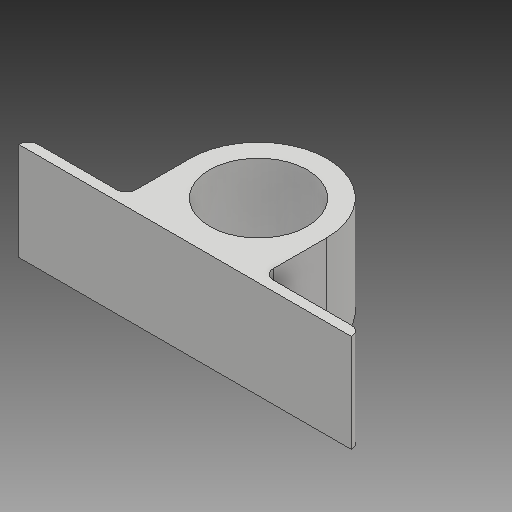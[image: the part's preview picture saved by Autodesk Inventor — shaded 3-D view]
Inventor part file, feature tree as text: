
AUTODESK INVENTOR PART (.ipt)
format: ipt  version: 2017 (Build 210142000, 142)  size: 120,832 bytes
history: native  units: mm
features: other x3, extrude x1, sketch x1, reference x1
ambient origin geometry x8: Origin, YZ Plane, XZ Plane, XY Plane, X Axis, Y Axis, Z Axis, Center Point
bodies: Solid1 (feature_tree)
feature tree (6):
  extrude  "Extrusion1"  Depth=2.0mm
  sketch  "Sketch1"  dims[d0=20.0mm d1=2.0mm d2=4.0mm d3=20.0mm d4=20.0mm d5=15.0mm d6=150.0mm d7=2.0mm d8=20.0mm d9=0.0mm]
  reference  "Reference1"
  parser-record x1  (decoder bookkeeping rows leaked as tree rows — omitted from the tree; the rows remain in map.json)
  other  "VolledigGeassembleerdv001.iam"
  other  "Frame:1"
note: 1 file-system path scrubbed to <path> (originals preserved in map.json)
